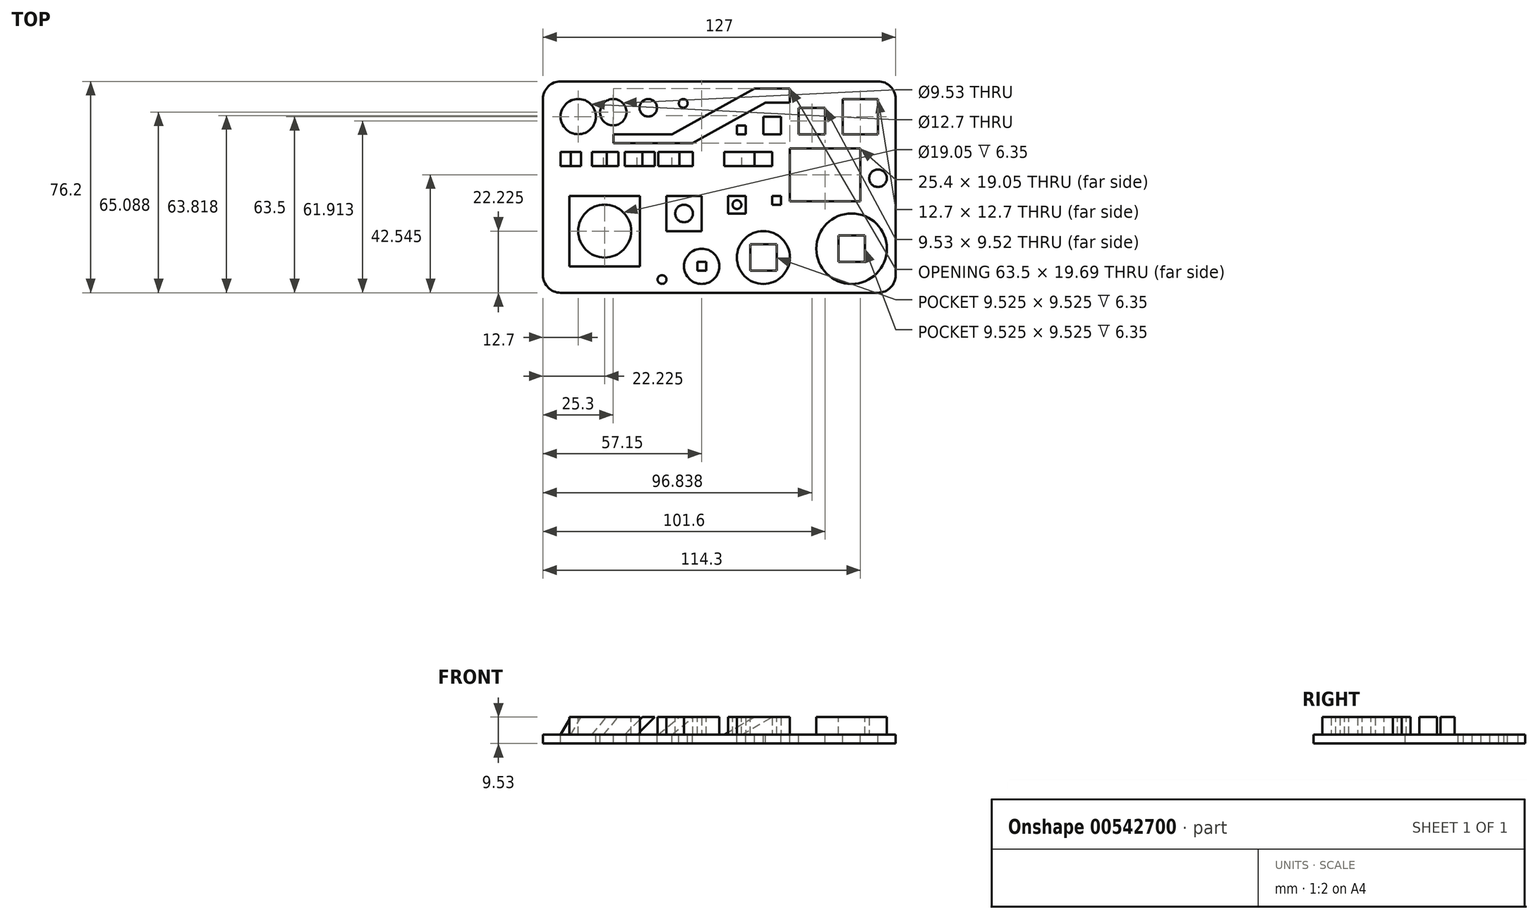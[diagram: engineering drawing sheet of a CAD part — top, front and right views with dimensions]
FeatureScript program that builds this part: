
annotation { "Feature Type Name" : "Feature", "Feature Type Description" : "" }
export const myFeature = defineFeature(function(context is Context, id is Id, definition is map)
    precondition{}
    {
        {
            var Q0;
            Q0=qCreatedBy(makeId("Top.planeOp"),FACE);
            var sketch = newSketch(context, id + "F0", { "sketchPlane" : qUnion([Q0])});
            skLineSegment(sketch, "E0.bottom", {"start": v(-63.5, 38.1) * mm, "end": v(63.5, 38.1) * mm});
            skLineSegment(sketch, "E0.top", {"start": v(-63.5, -38.1) * mm, "end": v(63.5, -38.1) * mm});
            skLineSegment(sketch, "E0.left", {"start": v(-63.5, 38.1) * mm, "end": v(-63.5, -38.1) * mm});
            skLineSegment(sketch, "E0.right", {"start": v(63.5, 38.1) * mm, "end": v(63.5, -38.1) * mm});
            skLineSegment(sketch, "E1", {"start": v(63.5, 38.1) * mm, "end": v(-63.5, -38.1) * mm, "construction": true});
            skSolve(sketch);
        }
        {
            var Q0;
            Q0 = qSketchRegion(id + "F0", true);
            extrude(context, id + "F1", {"entities" : qUnion([Q0]), "depth" : 3.17 * mm, "offsetDistance" : 25.4 * mm});
        }
        {
            var Q0;
            Q0=makeQuery(id+"F1.opExtrude","CAP_FACE",FACE,{"disambiguationData":[OSD([sQuery(id+"F0.wireOp",EDGE,"E0.bottom"),sQuery(id+"F0.wireOp",EDGE,"E0.top"),sQuery(id+"F0.wireOp",EDGE,"E0.left"),sQuery(id+"F0.wireOp",EDGE,"E0.right")])],"isStart":false});
            var sketch = newSketch(context, id + "F2", { "sketchPlane" : qUnion([Q0])});
            skCircle(sketch, "E2", {"center": v(-50.8, 25.4) * mm, "radius": 6.35 * mm});
            skCircle(sketch, "E3", {"center": v(-38.2, 26.99) * mm, "radius": 4.76 * mm});
            skCircle(sketch, "E4", {"center": v(-25.6, 28.58) * mm, "radius": 3.18 * mm});
            skCircle(sketch, "E5", {"center": v(-13, 30.16) * mm, "radius": 1.59 * mm});
            skLineSegment(sketch, "E6", {"start": v(-50.8, 25.4) * mm, "end": v(-18.64, 29.45) * mm});
            skLineSegment(sketch, "E7.bottom", {"start": v(57.15, 31.75) * mm, "end": v(44.45, 31.75) * mm});
            skLineSegment(sketch, "E7.top", {"start": v(57.15, 19.05) * mm, "end": v(44.45, 19.05) * mm});
            skLineSegment(sketch, "E7.left", {"start": v(57.15, 31.75) * mm, "end": v(57.15, 19.05) * mm});
            skLineSegment(sketch, "E7.right", {"start": v(44.45, 31.75) * mm, "end": v(44.45, 19.05) * mm});
            skLineSegment(sketch, "E8.bottom", {"start": v(38.1, 28.57) * mm, "end": v(28.58, 28.57) * mm});
            skLineSegment(sketch, "E8.top", {"start": v(38.1, 19.05) * mm, "end": v(28.58, 19.05) * mm});
            skLineSegment(sketch, "E8.left", {"start": v(38.1, 28.58) * mm, "end": v(38.1, 19.05) * mm});
            skLineSegment(sketch, "E8.right", {"start": v(28.58, 28.58) * mm, "end": v(28.58, 19.05) * mm});
            skLineSegment(sketch, "E9.bottom", {"start": v(22.23, 25.4) * mm, "end": v(15.87, 25.4) * mm});
            skLineSegment(sketch, "E9.top", {"start": v(22.23, 19.05) * mm, "end": v(15.88, 19.05) * mm});
            skLineSegment(sketch, "E9.left", {"start": v(22.23, 25.4) * mm, "end": v(22.23, 19.05) * mm});
            skLineSegment(sketch, "E9.right", {"start": v(15.88, 25.4) * mm, "end": v(15.88, 19.05) * mm});
            skLineSegment(sketch, "E10.bottom", {"start": v(9.53, 22.22) * mm, "end": v(6.35, 22.22) * mm});
            skLineSegment(sketch, "E10.top", {"start": v(9.52, 19.05) * mm, "end": v(6.35, 19.05) * mm});
            skLineSegment(sketch, "E10.left", {"start": v(9.53, 22.23) * mm, "end": v(9.53, 19.05) * mm});
            skLineSegment(sketch, "E10.right", {"start": v(6.35, 22.23) * mm, "end": v(6.35, 19.05) * mm});
            skLineSegment(sketch, "E11", {"start": v(-50.8, 31.75) * mm, "end": v(-15.92, 31.75) * mm, "construction": true});
            skSolve(sketch);
        }
        {
            var Q0;
            Q0 = qSketchRegion(id + "F2", true);
            extrude(context, id + "F3", {"entities" : qUnion([Q0]), "operationType" : NewBodyOperationType.REMOVE, "endBound" : BoundingType.UP_TO_NEXT, "oppositeDirection" : true, "depth" : 25.4 * mm, "offsetDistance" : 25.4 * mm});
        }
        {
            var Q0;
            Q0=makeQuery(id+"F1.opExtrude","CAP_FACE",FACE,{"disambiguationData":[OSD([sQuery(id+"F0.wireOp",EDGE,"E0.bottom"),sQuery(id+"F0.wireOp",EDGE,"E0.top"),sQuery(id+"F0.wireOp",EDGE,"E0.left"),sQuery(id+"F0.wireOp",EDGE,"E0.right")])],"isStart":false});
            var sketch = newSketch(context, id + "F4", { "sketchPlane" : qUnion([Q0])});
            skLineSegment(sketch, "E12.bottom", {"start": v(-53.98, -3.17) * mm, "end": v(-28.57, -3.17) * mm});
            skLineSegment(sketch, "E12.top", {"start": v(-53.98, -28.57) * mm, "end": v(-28.57, -28.57) * mm});
            skLineSegment(sketch, "E12.left", {"start": v(-53.98, -3.17) * mm, "end": v(-53.98, -28.57) * mm});
            skLineSegment(sketch, "E12.right", {"start": v(-28.57, -3.17) * mm, "end": v(-28.57, -28.57) * mm});
            skLineSegment(sketch, "E13.bottom", {"start": v(-19.05, -3.17) * mm, "end": v(-6.35, -3.17) * mm});
            skLineSegment(sketch, "E13.top", {"start": v(-19.05, -15.87) * mm, "end": v(-6.35, -15.87) * mm});
            skLineSegment(sketch, "E13.left", {"start": v(-19.05, -3.17) * mm, "end": v(-19.05, -15.87) * mm});
            skLineSegment(sketch, "E13.right", {"start": v(-6.35, -3.17) * mm, "end": v(-6.35, -15.87) * mm});
            skLineSegment(sketch, "E14.bottom", {"start": v(3.18, -3.17) * mm, "end": v(9.53, -3.17) * mm});
            skLineSegment(sketch, "E14.top", {"start": v(3.18, -9.52) * mm, "end": v(9.53, -9.52) * mm});
            skLineSegment(sketch, "E14.left", {"start": v(3.18, -3.17) * mm, "end": v(3.18, -9.53) * mm});
            skLineSegment(sketch, "E14.right", {"start": v(9.53, -3.17) * mm, "end": v(9.53, -9.52) * mm});
            skLineSegment(sketch, "E15.bottom", {"start": v(19.05, -3.17) * mm, "end": v(22.23, -3.17) * mm});
            skLineSegment(sketch, "E15.top", {"start": v(19.05, -6.35) * mm, "end": v(22.23, -6.35) * mm});
            skLineSegment(sketch, "E15.left", {"start": v(19.05, -3.17) * mm, "end": v(19.05, -6.35) * mm});
            skLineSegment(sketch, "E15.right", {"start": v(22.23, -3.17) * mm, "end": v(22.23, -6.35) * mm});
            skLineSegment(sketch, "E16", {"start": v(-28.57, -3.17) * mm, "end": v(-19.05, -3.17) * mm, "construction": true});
            skLineSegment(sketch, "E17", {"start": v(-6.35, -3.17) * mm, "end": v(3.18, -3.17) * mm, "construction": true});
            skLineSegment(sketch, "E18", {"start": v(9.53, -3.17) * mm, "end": v(19.05, -3.17) * mm, "construction": true});
            skSolve(sketch);
        }
        {
            var Q0;
            Q0 = qSketchRegion(id + "F4", true);
            extrude(context, id + "F5", {"entities" : qUnion([Q0]), "operationType" : NewBodyOperationType.ADD, "depth" : 6.35 * mm, "offsetDistance" : 25.4 * mm});
        }
        {
            var Q0;
            Q0=makeQuery(id+"F5.opExtrude","CAP_FACE",FACE,{"disambiguationData":[OSD([sQuery(id+"F4.wireOp",EDGE,"E12.bottom"),sQuery(id+"F4.wireOp",EDGE,"E12.top"),sQuery(id+"F4.wireOp",EDGE,"E12.left"),sQuery(id+"F4.wireOp",EDGE,"E12.right")])],"isStart":false});
            var sketch = newSketch(context, id + "F6", { "sketchPlane" : qUnion([Q0])});
            skCircle(sketch, "E19", {"center": v(-41.27, -15.87) * mm, "radius": 9.53 * mm});
            skPoint(sketch, "E19.centerSnap0", {"position": v(-28.57, -15.87) * mm});
            skPoint(sketch, "E19.centerSnap1", {"position": v(-41.27, -3.17) * mm});
            skCircle(sketch, "E20", {"center": v(-12.7, -9.52) * mm, "radius": 3.18 * mm});
            skCircle(sketch, "E21", {"center": v(6.35, -6.35) * mm, "radius": 1.59 * mm});
            skLineSegment(sketch, "E22", {"start": v(-41.27, -3.17) * mm, "end": v(-41.27, -15.87) * mm, "construction": true});
            skLineSegment(sketch, "E23", {"start": v(-28.57, -15.87) * mm, "end": v(-41.27, -15.87) * mm, "construction": true});
            skPoint(sketch, "E24.center.orphan", {"position": v(0, -27) * mm});
            skPoint(sketch, "E25.center.orphan", {"position": v(33.32, -22.89) * mm});
            skPoint(sketch, "E26.left.end.orphan", {"position": v(26.97, -29.24) * mm});
            skPoint(sketch, "E26.right.start.orphan", {"position": v(39.67, -16.54) * mm});
            skSolve(sketch);
        }
        {
            var Q0;
            Q0 = qSketchRegion(id + "F6", true);
            extrude(context, id + "F7", {"entities" : qUnion([Q0]), "operationType" : NewBodyOperationType.REMOVE, "oppositeDirection" : true, "depth" : 6.35 * mm, "offsetDistance" : 25.4 * mm});
        }
        {
            var Q0;
            Q0=makeQuery(id+"F1.opExtrude","CAP_FACE",FACE,{"disambiguationData":[OSD([sQuery(id+"F0.wireOp",EDGE,"E0.bottom"),sQuery(id+"F0.wireOp",EDGE,"E0.top"),sQuery(id+"F0.wireOp",EDGE,"E0.left"),sQuery(id+"F0.wireOp",EDGE,"E0.right")])],"isStart":false});
            var sketch = newSketch(context, id + "F8", { "sketchPlane" : qUnion([Q0])});
            skCircle(sketch, "E27", {"center": v(47.62, -22.22) * mm, "radius": 12.7 * mm});
            skCircle(sketch, "E28", {"center": v(-6.35, -28.57) * mm, "radius": 6.35 * mm});
            skPoint(sketch, "E29.right.start.orphan", {"position": v(-3.17, -25.4) * mm});
            skPoint(sketch, "E30.end.orphan", {"position": v(-9.53, -31.75) * mm});
            skPoint(sketch, "E31.right.start.orphan", {"position": v(53.97, -15.88) * mm});
            skPoint(sketch, "E31.top.end.orphan", {"position": v(28.57, -28.57) * mm});
            skPoint(sketch, "E32.end.orphan", {"position": v(41.28, -28.57) * mm});
            skCircle(sketch, "E33", {"center": v(15.87, -25.4) * mm, "radius": 9.53 * mm});
            skCircle(sketch, "E34", {"center": v(57.15, 3.18) * mm, "radius": 3.18 * mm});
            skCircle(sketch, "E35", {"center": v(-20.64, -33.34) * mm, "radius": 1.59 * mm});
            skSolve(sketch);
        }
        {
            var Q0;
            Q0 = qSketchRegion(id + "F8", true);
            extrude(context, id + "F9", {"entities" : qUnion([Q0]), "operationType" : NewBodyOperationType.ADD, "depth" : 6.35 * mm, "offsetDistance" : 25.4 * mm});
        }
        {
            var Q0;
            Q0=makeQuery(id+"F9.opExtrude","CAP_FACE",FACE,{"disambiguationData":[OSD([sQuery(id+"F8.wireOp",EDGE,"E27")])],"isStart":false});
            var sketch = newSketch(context, id + "F10", { "sketchPlane" : qUnion([Q0])});
            skLineSegment(sketch, "E36.bottom", {"start": v(42.86, -17.46) * mm, "end": v(52.39, -17.46) * mm});
            skLineSegment(sketch, "E36.top", {"start": v(42.86, -26.99) * mm, "end": v(52.39, -26.99) * mm});
            skLineSegment(sketch, "E36.left", {"start": v(42.86, -17.46) * mm, "end": v(42.86, -26.99) * mm});
            skLineSegment(sketch, "E36.right", {"start": v(52.39, -17.46) * mm, "end": v(52.39, -26.99) * mm});
            skLineSegment(sketch, "E37.bottom", {"start": v(11.11, -20.64) * mm, "end": v(20.64, -20.64) * mm});
            skLineSegment(sketch, "E37.top", {"start": v(11.11, -30.16) * mm, "end": v(20.64, -30.16) * mm});
            skLineSegment(sketch, "E37.left", {"start": v(11.11, -20.64) * mm, "end": v(11.11, -30.16) * mm});
            skLineSegment(sketch, "E37.right", {"start": v(20.64, -20.64) * mm, "end": v(20.64, -30.16) * mm});
            skLineSegment(sketch, "E38.bottom", {"start": v(-7.94, -26.99) * mm, "end": v(-4.76, -26.99) * mm});
            skLineSegment(sketch, "E38.top", {"start": v(-7.94, -30.16) * mm, "end": v(-4.76, -30.16) * mm});
            skLineSegment(sketch, "E38.left", {"start": v(-7.94, -26.99) * mm, "end": v(-7.94, -30.16) * mm});
            skLineSegment(sketch, "E38.right", {"start": v(-4.76, -26.99) * mm, "end": v(-4.76, -30.16) * mm});
            skCircle(sketch, "E39.0", {"center": v(-6.35, -28.57) * mm, "radius": 6.35 * mm, "construction": true});
            skCircle(sketch, "E40.0", {"center": v(15.87, -25.4) * mm, "radius": 9.53 * mm, "construction": true});
            skCircle(sketch, "E41.0", {"center": v(47.62, -22.22) * mm, "radius": 12.7 * mm, "construction": true});
            skLineSegment(sketch, "E42", {"start": v(15.87, -15.87) * mm, "end": v(15.87, -34.92) * mm, "construction": true});
            skLineSegment(sketch, "E43", {"start": v(-12.7, -28.57) * mm, "end": v(0, -28.57) * mm, "construction": true});
            skLineSegment(sketch, "E44", {"start": v(-6.34, -22.23) * mm, "end": v(-6.34, -34.92) * mm, "construction": true});
            skLineSegment(sketch, "E45", {"start": v(6.35, -25.4) * mm, "end": v(25.4, -25.4) * mm, "construction": true});
            skLineSegment(sketch, "E46", {"start": v(34.92, -22.22) * mm, "end": v(60.33, -22.22) * mm, "construction": true});
            skLineSegment(sketch, "E47", {"start": v(47.62, -9.52) * mm, "end": v(47.62, -34.92) * mm, "construction": true});
            skLineSegment(sketch, "E48", {"start": v(-4.76, -26.99) * mm, "end": v(-7.94, -30.16) * mm, "construction": true});
            skLineSegment(sketch, "E49", {"start": v(11.11, -30.16) * mm, "end": v(20.64, -20.64) * mm});
            skLineSegment(sketch, "E50", {"start": v(52.39, -17.46) * mm, "end": v(42.86, -26.99) * mm});
            skSolve(sketch);
        }
        {
            var Q0;
            Q0 = qSketchRegion(id + "F10", true);
            extrude(context, id + "F11", {"entities" : qUnion([Q0]), "operationType" : NewBodyOperationType.REMOVE, "oppositeDirection" : true, "depth" : 6.35 * mm, "offsetDistance" : 25.4 * mm});
        }
        {
            var Q0;
            Q0=makeQuery(id+"F1.opExtrude","CAP_FACE",FACE,{"disambiguationData":[OSD([sQuery(id+"F0.wireOp",EDGE,"E0.bottom"),sQuery(id+"F0.wireOp",EDGE,"E0.top"),sQuery(id+"F0.wireOp",EDGE,"E0.left"),sQuery(id+"F0.wireOp",EDGE,"E0.right")])],"isStart":false});
            var sketch = newSketch(context, id + "F12", { "sketchPlane" : qUnion([Q0])});
            skLineSegment(sketch, "E51.bottom", {"start": v(-57.15, 12.7) * mm, "end": v(19.05, 12.7) * mm});
            skLineSegment(sketch, "E51.top", {"start": v(-57.15, 7.62) * mm, "end": v(19.05, 7.62) * mm});
            skLineSegment(sketch, "E51.left", {"start": v(-57.15, 12.7) * mm, "end": v(-57.15, 7.62) * mm});
            skLineSegment(sketch, "E51.right", {"start": v(19.05, 12.7) * mm, "end": v(19.05, 7.62) * mm});
            skSolve(sketch);
        }
        {
            var Q0;
            Q0 = qSketchRegion(id + "F12", true);
            extrude(context, id + "F13", {"entities" : qUnion([Q0]), "operationType" : NewBodyOperationType.ADD, "depth" : 6.35 * mm, "offsetDistance" : 25.4 * mm});
        }
        {
            var Q0;
            Q0=makeQuery(id+"F13.opExtrude","SWEPT_FACE",FACE,{"disambiguationData":[OSD([sQuery(id+"F12.wireOp",EDGE,"E51.bottom")])]});
            var sketch = newSketch(context, id + "F14", { "sketchPlane" : qUnion([Q0])});
            skLineSegment(sketch, "E52", {"start": v(57.15, 3.18) * mm, "end": v(53.48, 9.53) * mm});
            skPoint(sketch, "E53.0.end.orphan", {"position": v(57.15, 3.18) * mm});
            skPoint(sketch, "E53.0.start.orphan", {"position": v(57.15, 9.53) * mm});
            skLineSegment(sketch, "E54.0", {"start": v(53.48, 3.18) * mm, "end": v(49.82, 9.53) * mm});
            skLineSegment(sketch, "E55", {"start": v(45.86, 3.18) * mm, "end": v(40.54, 9.53) * mm});
            skLineSegment(sketch, "E56.0", {"start": v(41.72, 3.17) * mm, "end": v(36.4, 9.53) * mm});
            skLineSegment(sketch, "E57", {"start": v(34.1, 3.18) * mm, "end": v(27.75, 9.53) * mm});
            skLineSegment(sketch, "E58", {"start": v(21.99, 3.17) * mm, "end": v(14.42, 9.52) * mm});
            skLineSegment(sketch, "E59.0", {"start": v(29.6, 3.17) * mm, "end": v(23.26, 9.53) * mm});
            skLineSegment(sketch, "E60.0", {"start": v(17.05, 3.17) * mm, "end": v(9.48, 9.53) * mm});
            skLineSegment(sketch, "E61", {"start": v(-1.7, 3.17) * mm, "end": v(-12.7, 9.53) * mm});
            skLineSegment(sketch, "E62.0", {"start": v(-8.05, 3.17) * mm, "end": v(-19.05, 9.53) * mm});
            skLineSegment(sketch, "E63", {"start": v(-19.05, 9.53) * mm, "end": v(-19.05, 3.18) * mm});
            skLineSegment(sketch, "E64", {"start": v(-19.05, 3.18) * mm, "end": v(-8.05, 3.18) * mm});
            skLineSegment(sketch, "E65", {"start": v(57.15, 9.53) * mm, "end": v(57.15, 3.18) * mm});
            skLineSegment(sketch, "E66", {"start": v(57.15, 9.53) * mm, "end": v(53.48, 9.53) * mm});
            skLineSegment(sketch, "E67.trimOffspring", {"start": v(9.48, 9.53) * mm, "end": v(-12.7, 9.53) * mm});
            skLineSegment(sketch, "E68.trimOffspring", {"start": v(21.99, 3.18) * mm, "end": v(29.6, 3.18) * mm});
            skLineSegment(sketch, "E69.trimOffspring", {"start": v(-1.7, 3.18) * mm, "end": v(17.05, 3.18) * mm});
            skLineSegment(sketch, "E70.trimOffspring", {"start": v(49.82, 9.53) * mm, "end": v(40.54, 9.53) * mm});
            skLineSegment(sketch, "E71.trimOffspring", {"start": v(34.1, 3.18) * mm, "end": v(41.72, 3.18) * mm});
            skLineSegment(sketch, "E72.trimOffspring", {"start": v(45.86, 3.18) * mm, "end": v(53.48, 3.18) * mm});
            skLineSegment(sketch, "E73", {"start": v(14.42, 9.52) * mm, "end": v(23.26, 9.53) * mm});
            skLineSegment(sketch, "E74", {"start": v(27.75, 9.53) * mm, "end": v(36.4, 9.53) * mm});
            skSolve(sketch);
        }
        {
            var Q0;
            Q0 = qSketchRegion(id + "F14", true);
            extrude(context, id + "F15", {"entities" : qUnion([Q0]), "operationType" : NewBodyOperationType.REMOVE, "endBound" : BoundingType.UP_TO_NEXT, "oppositeDirection" : true, "depth" : 25.4 * mm, "offsetDistance" : 25.4 * mm});
        }
        {
            var Q0;
            Q0=makeQuery(id+"F1.opExtrude","SWEPT_EDGE",EDGE,{"disambiguationData":[OSD([sQuery(id+"F0.wireOp",EDGE,"E0.top"),sQuery(id+"F0.wireOp",EDGE,"E0.right")])]});
            var Q1;
            Q1=makeQuery(id+"F1.opExtrude","SWEPT_EDGE",EDGE,{"disambiguationData":[OSD([sQuery(id+"F0.wireOp",EDGE,"E0.top"),sQuery(id+"F0.wireOp",EDGE,"E0.left")])]});
            var Q2;
            Q2=makeQuery(id+"F1.opExtrude","SWEPT_EDGE",EDGE,{"disambiguationData":[OSD([sQuery(id+"F0.wireOp",EDGE,"E0.bottom"),sQuery(id+"F0.wireOp",EDGE,"E0.left")])]});
            var Q3;
            Q3=makeQuery(id+"F1.opExtrude","SWEPT_EDGE",EDGE,{"disambiguationData":[OSD([sQuery(id+"F0.wireOp",EDGE,"E0.bottom"),sQuery(id+"F0.wireOp",EDGE,"E0.right")])]});
            fillet(context, id + "F16", {"entities" : qUnion([Q0, Q1, Q2, Q3]), "radius" : 6.35 * mm, "tangentPropagation" : true, "allowEdgeOverflow" : false});
        }
        {
            var Q0;
            Q0=makeQuery(id+"F15.boolean.opBoolean","MERGE",FACE,{"derivedFrom":[makeQuery(id+"F1.opExtrude","CAP_FACE",FACE,{"disambiguationData":[OSD([sQuery(id+"F0.wireOp",EDGE,"E0.bottom"),sQuery(id+"F0.wireOp",EDGE,"E0.top"),sQuery(id+"F0.wireOp",EDGE,"E0.left"),sQuery(id+"F0.wireOp",EDGE,"E0.right")])],"isStart":false}),makeQuery(id+"F15.opExtrude","SWEPT_FACE",FACE,{"disambiguationData":[OSD([sQuery(id+"F14.wireOp",EDGE,"E64")])]}),makeQuery(id+"F15.opExtrude","SWEPT_FACE",FACE,{"disambiguationData":[OSD([sQuery(id+"F14.wireOp",EDGE,"E68.trimOffspring")])]}),makeQuery(id+"F15.opExtrude","SWEPT_FACE",FACE,{"disambiguationData":[OSD([sQuery(id+"F14.wireOp",EDGE,"E69.trimOffspring")])]}),makeQuery(id+"F15.opExtrude","SWEPT_FACE",FACE,{"disambiguationData":[OSD([sQuery(id+"F14.wireOp",EDGE,"E71.trimOffspring")])]}),makeQuery(id+"F15.opExtrude","SWEPT_FACE",FACE,{"disambiguationData":[OSD([sQuery(id+"F14.wireOp",EDGE,"E72.trimOffspring")])]})]});
            var sketch = newSketch(context, id + "F17", { "sketchPlane" : qUnion([Q0])});
            skLineSegment(sketch, "E75", {"start": v(16.63, 30.48) * mm, "end": v(-9.66, 15.88) * mm});
            skLineSegment(sketch, "E76", {"start": v(-17.02, 19.05) * mm, "end": v(12.7, 35.56) * mm});
            skLineSegment(sketch, "E77", {"start": v(12.7, 35.56) * mm, "end": v(25.4, 35.56) * mm});
            skLineSegment(sketch, "E78", {"start": v(25.4, 35.56) * mm, "end": v(25.4, 30.48) * mm});
            skLineSegment(sketch, "E79", {"start": v(25.4, 30.48) * mm, "end": v(16.63, 30.48) * mm});
            skLineSegment(sketch, "E80", {"start": v(-17.02, 19.05) * mm, "end": v(-38.1, 19.05) * mm});
            skLineSegment(sketch, "E81", {"start": v(-38.1, 19.05) * mm, "end": v(-38.1, 15.88) * mm});
            skLineSegment(sketch, "E82", {"start": v(-38.1, 15.88) * mm, "end": v(-9.66, 15.88) * mm});
            skSolve(sketch);
        }
        {
            var Q0;
            Q0 = qSketchRegion(id + "F17", true);
            extrude(context, id + "F18", {"entities" : qUnion([Q0]), "operationType" : NewBodyOperationType.REMOVE, "endBound" : BoundingType.UP_TO_NEXT, "oppositeDirection" : true, "depth" : 25.4 * mm, "offsetDistance" : 25.4 * mm});
        }
        {
            var Q0;
            Q0=makeQuery(id+"F15.boolean.opBoolean","MERGE",FACE,{"derivedFrom":[makeQuery(id+"F1.opExtrude","CAP_FACE",FACE,{"disambiguationData":[OSD([sQuery(id+"F0.wireOp",EDGE,"E0.bottom"),sQuery(id+"F0.wireOp",EDGE,"E0.top"),sQuery(id+"F0.wireOp",EDGE,"E0.left"),sQuery(id+"F0.wireOp",EDGE,"E0.right")])],"isStart":false}),makeQuery(id+"F15.opExtrude","SWEPT_FACE",FACE,{"disambiguationData":[OSD([sQuery(id+"F14.wireOp",EDGE,"E64")])]}),makeQuery(id+"F15.opExtrude","SWEPT_FACE",FACE,{"disambiguationData":[OSD([sQuery(id+"F14.wireOp",EDGE,"E68.trimOffspring")])]}),makeQuery(id+"F15.opExtrude","SWEPT_FACE",FACE,{"disambiguationData":[OSD([sQuery(id+"F14.wireOp",EDGE,"E69.trimOffspring")])]}),makeQuery(id+"F15.opExtrude","SWEPT_FACE",FACE,{"disambiguationData":[OSD([sQuery(id+"F14.wireOp",EDGE,"E71.trimOffspring")])]}),makeQuery(id+"F15.opExtrude","SWEPT_FACE",FACE,{"disambiguationData":[OSD([sQuery(id+"F14.wireOp",EDGE,"E72.trimOffspring")])]})]});
            var sketch = newSketch(context, id + "F19", { "sketchPlane" : qUnion([Q0])});
            skLineSegment(sketch, "E83.bottom", {"start": v(50.8, -5.08) * mm, "end": v(25.4, -5.08) * mm});
            skLineSegment(sketch, "E83.top", {"start": v(50.8, 13.97) * mm, "end": v(25.4, 13.97) * mm});
            skLineSegment(sketch, "E83.left", {"start": v(50.8, -5.08) * mm, "end": v(50.8, 13.97) * mm});
            skLineSegment(sketch, "E83.right", {"start": v(25.4, -5.08) * mm, "end": v(25.4, 13.97) * mm});
            skSolve(sketch);
        }
        {
            var Q0;
            Q0 = qSketchRegion(id + "F19", true);
            extrude(context, id + "F20", {"entities" : qUnion([Q0]), "operationType" : NewBodyOperationType.REMOVE, "endBound" : BoundingType.UP_TO_NEXT, "oppositeDirection" : true, "depth" : 25.4 * mm, "offsetDistance" : 25.4 * mm});
        }
    });
